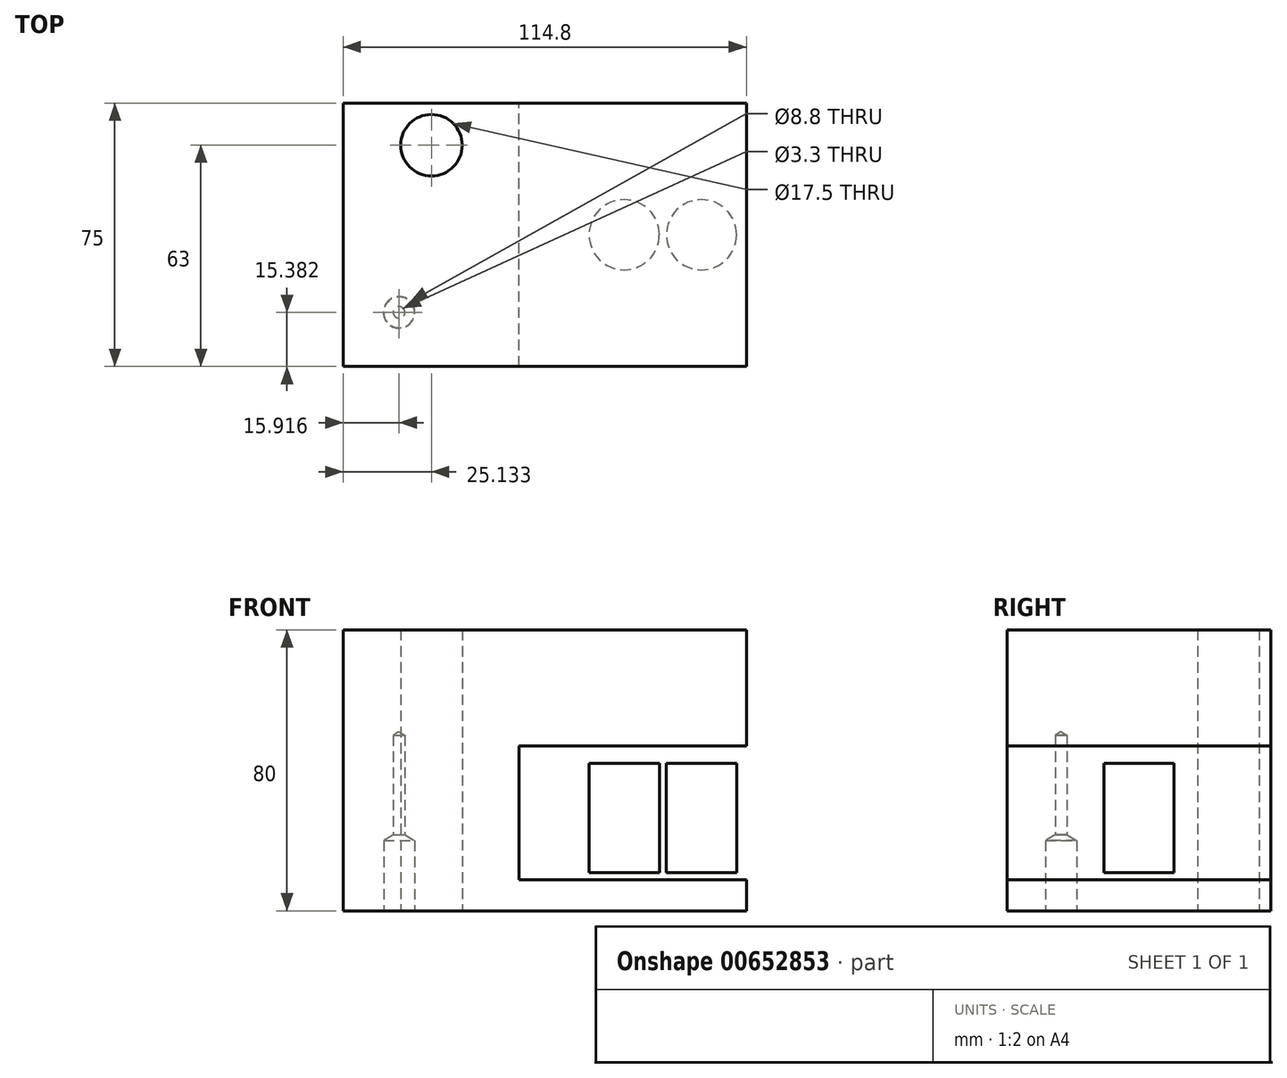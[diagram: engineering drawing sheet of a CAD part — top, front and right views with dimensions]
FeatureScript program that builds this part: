
annotation { "Feature Type Name" : "Feature", "Feature Type Description" : "" }
export const myFeature = defineFeature(function(context is Context, id is Id, definition is map)
    precondition{}
    {
        {
            var Q0;
            Q0=qCreatedBy(makeId("Top.planeOp"),FACE);
            var sketch = newSketch(context, id + "F0", { "sketchPlane" : qUnion([Q0])});
            skLineSegment(sketch, "E0.bottom", {"start": v(50, 37.5) * mm, "end": v(-50, 37.5) * mm});
            skLineSegment(sketch, "E0.top", {"start": v(50, -37.5) * mm, "end": v(-50, -37.5) * mm});
            skLineSegment(sketch, "E0.left", {"start": v(50, 37.5) * mm, "end": v(50, -37.5) * mm});
            skLineSegment(sketch, "E0.right", {"start": v(-50, 37.5) * mm, "end": v(-50, -37.5) * mm});
            skPoint(sketch, "E0.middle", {"position": v(0, 0) * mm});
            skPoint(sketch, "E1", {"position": v(-34.08, -22.12) * mm});
            skPoint(sketch, "E2", {"position": v(-24.87, 25.5) * mm});
            skPoint(sketch, "E3", {"position": v(40, 25.5) * mm});
            skPoint(sketch, "E4", {"position": v(40, -24.5) * mm});
            skPoint(sketch, "E5", {"position": v(0, -37.5) * mm});
            skPoint(sketch, "E6", {"position": v(0, 37.5) * mm});
            skLineSegment(sketch, "E7", {"start": v(-50, 0) * mm, "end": v(50, 0) * mm, "construction": true});
            skLineSegment(sketch, "E8", {"start": v(0, -37.5) * mm, "end": v(0, 37.5) * mm});
            skCircle(sketch, "E9", {"center": v(20, 17.5) * mm, "radius": 10 * mm});
            skSolve(sketch);
        }
        {
            var Q0;
            Q0=makeQuery(id+"F0.imprint","IMPRINT",FACE,{"disambiguationData":[TD([[makeQuery(id+"F0.imprint","IMPRINT",EDGE,{"derivedFrom":sQuery(id+"F0.wireOp",EDGE,"E0.bottom")}),1.0]])]});
            extrude(context, id + "F1", {"entities" : qUnion([Q0]), "depth" : 80 * mm, "offsetDistance" : 25 * mm});
        }
        {
            var Q0;
            Q0=sQuery(id+"F0.wireOp",VERTEX,"E1");
            var Q1;
            Q1=sQuery(id+"F0.wireOp",VERTEX,"E4");
            var Q2;
            Q2=sQuery(id+"F0.wireOp",VERTEX,"E3");
            var Q3;
            Q3=sQuery(id+"F0.wireOp",VERTEX,"E2");
            var Q4;
            Q4=makeQuery(id+"F1.opExtrude","SWEPT_BODY",BODY,{"disambiguationData":[OSD([sQuery(id+"F0.wireOp",EDGE,"E0.bottom"),sQuery(id+"F0.wireOp",EDGE,"E0.top"),sQuery(id+"F0.wireOp",EDGE,"E0.left"),sQuery(id+"F0.wireOp",EDGE,"E0.right")])]});
            hole(context, id + "F2", {"style" : HoleStyle.C_SINK, "endStyle" : HoleEndStyle.BLIND, "oppositeDirection" : true, "standardTappedOrClearance" : lookupTablePath({ "standard" : "ISO", "engagement" : "75%", "pitch" : "0.7 mm", "size" : "M4", "type" : "Tapped" }), "standardBlindInLast" : lookupTablePath({ "standard" : "ISO", "engagement" : "75%", "pitch" : "0.7 mm", "size" : "M4", "type" : "Tapped" }), "holeDiameter" : 3.3 * mm, "cSinkDiameter" : 8.96 * mm, "cSinkAngle" : 90 * degree, "majorDiameter" : 4 * mm, "showTappedDepth" : true, "holeDepth" : 50 * mm, "tappedDepth" : 47.9 * mm, "tapClearance" : 3, "locations" : qUnion([Q0, Q1, Q2, Q3]), "scope" : qUnion([Q4])});
        }
        {
            var Q0;
            Q0=sQuery(id+"F0.wireOp",VERTEX,"E1");
            var Q1;
            Q1=makeQuery(id+"F1.opExtrude","SWEPT_BODY",BODY,{"disambiguationData":[OSD([sQuery(id+"F0.wireOp",EDGE,"E0.bottom"),sQuery(id+"F0.wireOp",EDGE,"E0.top"),sQuery(id+"F0.wireOp",EDGE,"E0.right"),sQuery(id+"F0.wireOp",EDGE,"E8")])]});
            hole(context, id + "F3", {"style" : HoleStyle.SIMPLE, "endStyle" : HoleEndStyle.BLIND, "oppositeDirection" : true, "holeDiameter" : 8.8 * mm, "majorDiameter" : 5 * mm, "holeDepth" : 20 * mm, "tappedDepth" : 66.25 * mm, "tapClearance" : 3, "startFromSketch" : true, "locations" : qUnion([Q0]), "scope" : qUnion([Q1])});
        }
        {
            var Q0;
            Q0=sQuery(id+"F0.wireOp",VERTEX,"E2");
            var Q1;
            Q1=makeQuery(id+"F1.opExtrude","SWEPT_BODY",BODY,{"disambiguationData":[OSD([sQuery(id+"F0.wireOp",EDGE,"E0.bottom"),sQuery(id+"F0.wireOp",EDGE,"E0.top"),sQuery(id+"F0.wireOp",EDGE,"E0.right"),sQuery(id+"F0.wireOp",EDGE,"E8")])]});
            hole(context, id + "F4", {"style" : HoleStyle.SIMPLE, "endStyle" : HoleEndStyle.THROUGH, "oppositeDirection" : true, "standardTappedOrClearance" : lookupTablePath({ "standard" : "ISO", "engagement" : "75%", "pitch" : "2.5 mm", "size" : "M20", "type" : "Tapped" }), "standardBlindInLast" : lookupTablePath({ "standard" : "ISO", "engagement" : "75%", "pitch" : "2.5 mm", "size" : "M20", "type" : "Tapped" }), "holeDiameter" : 17.5 * mm, "majorDiameter" : 20 * mm, "showTappedDepth" : true, "isTappedThrough" : true, "tappedDepth" : 66.25 * mm, "tapClearance" : 3, "startFromSketch" : true, "locations" : qUnion([Q0]), "scope" : qUnion([Q1])});
        }
        {
            var Q0;
            Q0=makeQuery(id+"F1.opExtrude","SWEPT_FACE",FACE,{"disambiguationData":[OSD([sQuery(id+"F0.wireOp",EDGE,"E8")])]});
            var sketch = newSketch(context, id + "F5", { "sketchPlane" : qUnion([Q0])});
            skLineSegment(sketch, "E10", {"start": v(-37.5, 47) * mm, "end": v(37.5, 47) * mm});
            skLineSegment(sketch, "E11", {"start": v(-37.5, 8.9) * mm, "end": v(37.5, 8.9) * mm});
            skSolve(sketch);
        }
        {
            var Q0;
            Q0 = qSketchRegion(id + "F5", true);
            var Q1;
            {var subQ0=sQuery(id+"F5.wireOp",EDGE,"E10");Q1=makeQuery(id+"F5.imprint","IMPRINT",FACE,{"disambiguationData":[TD([[makeQuery(id+"F5.imprint","IMPRINT",EDGE,{"derivedFrom":subQ0}),1.0]])]});}
            var Q2;
            {var subQ0=sQuery(id+"F5.wireOp",EDGE,"E11");Q2=makeQuery(id+"F5.imprint","IMPRINT",FACE,{"disambiguationData":[TD([[makeQuery(id+"F5.imprint","IMPRINT",EDGE,{"derivedFrom":subQ0}),-1.0]])]});}
            extrude(context, id + "F6", {"entities" : qUnion([Q0, Q1, Q2]), "operationType" : NewBodyOperationType.ADD, "depth" : 64.8 * mm, "offsetDistance" : 25 * mm});
        }
        {
            var Q0;
            Q0=makeQuery(id+"F6.opExtrude","SWEPT_FACE",FACE,{"disambiguationData":[OSD([sQuery(id+"F5.wireOp",EDGE,"E11")])]});
            var Q1;
            Q1=makeQuery(id+"F6.opExtrude","SWEPT_FACE",FACE,{"disambiguationData":[OSD([sQuery(id+"F5.wireOp",EDGE,"E10")])]});
            cPlane(context, id + "F7", {"entities" : qUnion([Q0, Q1]), "cplaneType" : CPlaneType.MID_PLANE, "offset" : 25 * mm, "width" : 150 * mm, "height" : 150 * mm});
        }
        {
            var Q0;
            Q0=qCreatedBy(id+"F7.planeOp",FACE);
            var sketch = newSketch(context, id + "F8", { "sketchPlane" : qUnion([Q0])});
            skCircle(sketch, "E12", {"center": v(30, 0) * mm, "radius": 10 * mm});
            skSolve(sketch);
        }
        {
            var Q0;
            Q0=makeQuery(id+"F8.imprint","IMPRINT",FACE,{"disambiguationData":[TD([[makeQuery(id+"F8.imprint","IMPRINT",EDGE,{"derivedFrom":sQuery(id+"F8.wireOp",EDGE,"E12")}),1.0]])]});
            extrude(context, id + "F9", {"entities" : qUnion([Q0]), "endBound" : BoundingType.UP_TO_NEXT, "depth" : 25 * mm, "hasOffset" : true, "offsetDistance" : 5 * mm, "hasSecondDirection" : true, "secondDirectionBound" : SecondDirectionBoundingType.UP_TO_NEXT, "secondDirectionOppositeDirection" : true, "secondDirectionDepth" : 1 * mm, "hasSecondDirectionOffset" : true, "secondDirectionOffsetDistance" : 2 * mm});
        }
        {
            var Q0;
            Q0=makeQuery(id+"F9.opExtrude","SWEPT_BODY",BODY,{"disambiguationData":[OSD([sQuery(id+"F8.wireOp",EDGE,"E12")])]});
            transform(context, id + "F10", {"entities" : qUnion([Q0]), "transformType" : TransformType.TRANSLATION_3D, "dx" : 22 * mm, "dy" : 0 * mm, "dz" : 0 * mm, "makeCopy" : true});
        }
    });
